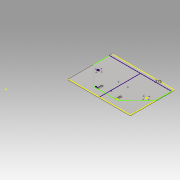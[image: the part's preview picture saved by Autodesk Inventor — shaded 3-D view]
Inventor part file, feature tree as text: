
AUTODESK INVENTOR PART (.ipt)
format: ipt  version: 2016 (Build 200138000, 138)  size: 220,160 bytes
history: native  units: in
note: dims shown in document units (in); Inventor stores cm internally (conversion verified against a paired STEP export)
features: sketch x7, extrude x4, hole x3
ambient origin geometry x8: Origin, YZ Plane, XZ Plane, XY Plane, X Axis, Y Axis, Z Axis, Center Point
bodies: Solid1 (feature_tree)
feature tree (14):
  extrude  "Extrusion1"  Depth=6.0in
  hole  "Hole1"  [1 undecoded]
  extrude  "Extrusion3"  Depth=3.1102in
  extrude  "Extrusion4"  Depth=1.0768in
  extrude  "Extrusion5"  Depth=1.0236in
  hole  "Hole2"  [1 undecoded]
  hole  "Hole4"  [1 undecoded]
  sketch  "Sketch15"  dims[d43=1.0in d44=0.0in d45=1.75in d47=1.75in d48=1.75in d49=1.75in d50=2.382in d52=2.5591in d53=0.6398in d54=0.6398in d55=2.382in d58=2.0472in d62=1.2795in d64=0.1181in d65=0.75in d66=0.375in d67=0.25in d68=0.5635in d69=1.0in d70=0.8108in d76=0.236in d77=0.492in d78=0.236in d79=0.492in d80=1.0in d81=0.0in d82=0.236in d83=0.492in d84=0.236in d85=0.492in d86=1.0in d87=0.0in d88=0.25in d125=0.0in d159=1.5748in d161=360.0deg d167=0.107in d168=0.75in d169=0.375in d170=0.25in d171=0.5635in d172=1.0in d173=0.8108in d174=0.7664in d175=0.7664in d176=1.5748in d178=360.0deg d180=2.5591in d181=1.2795in d186=2.5165in d192=0.25in d193=0.2953in d197=0.125in d198=0.125in d200=0.375in d201=1.4331in d202=1.126in]
  sketch  "Sketch1"  dims[d0=8.5in d1=6.0in]
  sketch  "Sketch3"  dims[d2=0.125in d3=0.0in d4=5.6831in]
  sketch  "Sketch5"  dims[d5=1.0236in d7=3.1102in]
  sketch  "Sketch7"  dims[d12=0.25in d13=0.75in d14=0.375in d15=0.25in d16=0.5635in d17=1.0in d18=0.8108in d19=1.0768in]
  sketch  "Sketch8"  dims[d20=3.1102in d21=1.0236in]
  sketch  "Sketch11"  dims[d22=3.124in d23=7.5728in]
note: 3 required parameter values undecoded (feature->parameter linkage not recoverable at this tier; creation-order binding heuristic only, values carry confidence <= 0.55)
